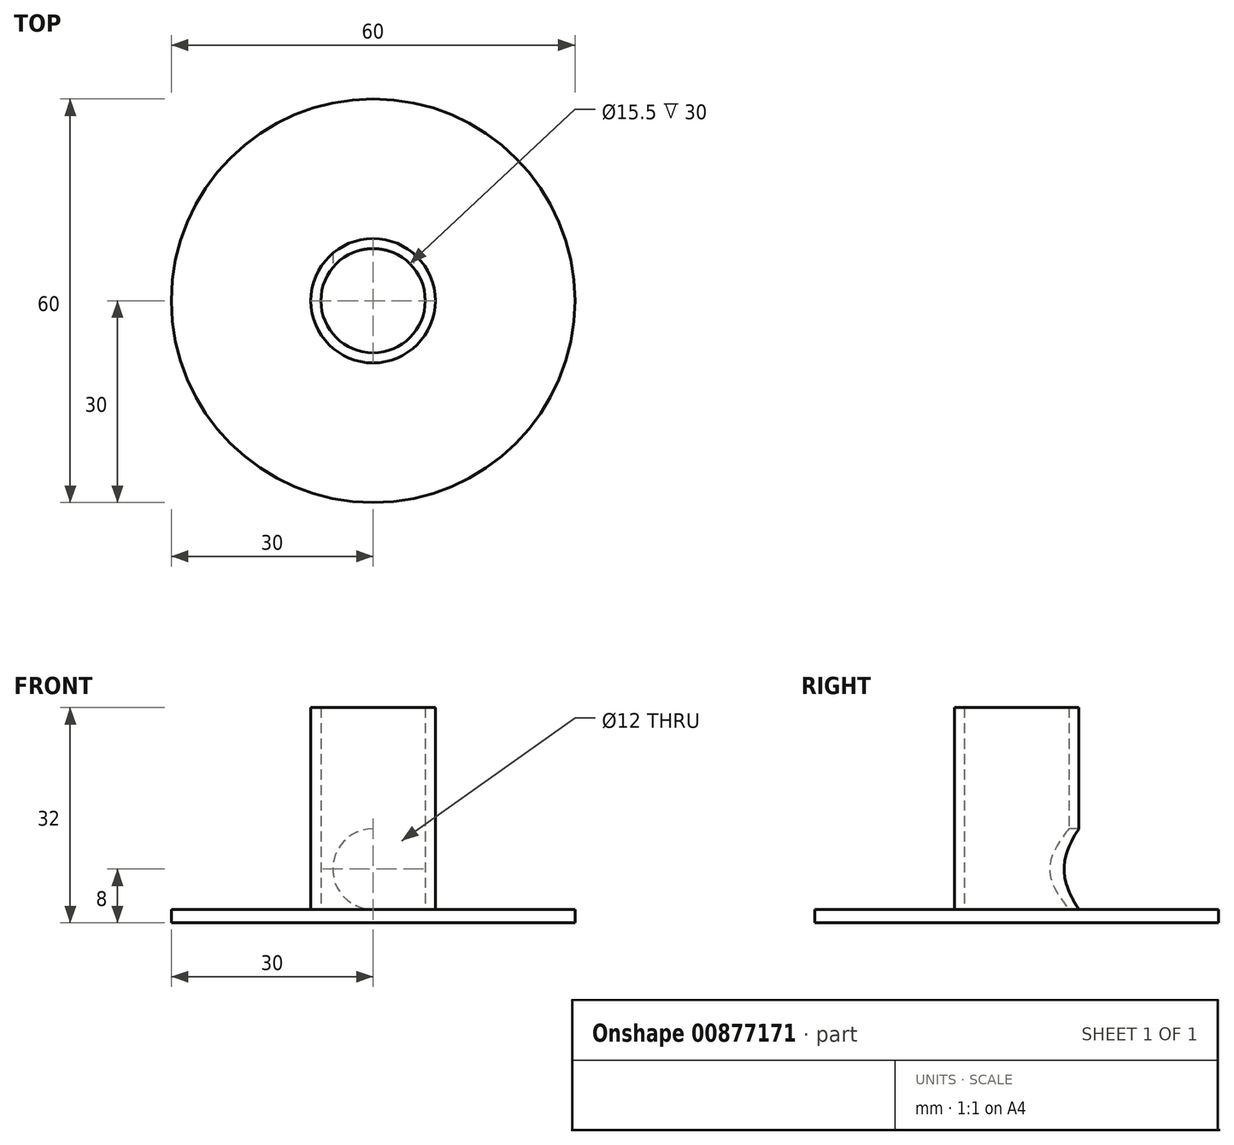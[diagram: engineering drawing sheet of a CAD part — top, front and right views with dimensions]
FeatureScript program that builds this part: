
annotation { "Feature Type Name" : "Feature", "Feature Type Description" : "" }
export const myFeature = defineFeature(function(context is Context, id is Id, definition is map)
    precondition{}
    {
        {
            var Q0;
            Q0=qCreatedBy(makeId("Top.planeOp"),FACE);
            var sketch = newSketch(context, id + "F0", { "sketchPlane" : qUnion([Q0])});
            skCircle(sketch, "E0", {"center": v(0, 0) * mm, "radius": 7.75 * mm});
            skCircle(sketch, "E1", {"center": v(0, 0) * mm, "radius": 9.25 * mm});
            skSolve(sketch);
        }
        {
            var Q0;
            Q0 = qSketchRegion(id + "F0", true);
            extrude(context, id + "F1", {"entities" : qUnion([Q0]), "depth" : 30 * mm, "offsetDistance" : 25 * mm});
        }
        {
            var Q0;
            Q0=makeQuery(id+"F1.opExtrude","CAP_FACE",FACE,{"disambiguationData":[OSD([sQuery(id+"F0.wireOp",EDGE,"E0"),sQuery(id+"F0.wireOp",EDGE,"E1")])],"isStart":true});
            var sketch = newSketch(context, id + "F2", { "sketchPlane" : qUnion([Q0])});
            skCircle(sketch, "E2", {"center": v(0, 0) * mm, "radius": 30 * mm});
            skSolve(sketch);
        }
        {
            var Q0;
            Q0 = qSketchRegion(id + "F2", true);
            extrude(context, id + "F3", {"entities" : qUnion([Q0]), "operationType" : NewBodyOperationType.ADD, "depth" : 2 * mm, "offsetDistance" : 25 * mm});
        }
        {
            var Q0;
            Q0=qCreatedBy(makeId("Front.planeOp"),FACE);
            var sketch = newSketch(context, id + "F4", { "sketchPlane" : qUnion([Q0])});
            skCircle(sketch, "E3", {"center": v(0, 6) * mm, "radius": 6 * mm});
            skSolve(sketch);
        }
        {
            var Q0;
            Q0 = qSketchRegion(id + "F4", true);
            extrude(context, id + "F5", {"entities" : qUnion([Q0]), "operationType" : NewBodyOperationType.REMOVE, "oppositeDirection" : true, "depth" : 25 * mm, "offsetDistance" : 25 * mm});
        }
    });
